# Revit family: Gira_289300
name_source: partatom
category: Electrical Fixtures
revit_build: Autodesk Revit 2017 (Build: 20160225_1515(x64)
units: mm (PartAtom-declared; Revit-internal decimal feet)

## family parameters
Cut with Voids When Loaded = No
Host = Face
Maintain Annotation Orientation = No
Part Type = Normal
Room Calculation Point = No
Round Connector Dimension = Use Diameter
Shared = No

## types (1)
- FM install.box 3-g Gira E22
    Available = No
    BIM (1) = https://media.stage.bim.site
    Category = Spare part for domestic switching devices
    Data sheet (1) = https://katalog.gira.de
    Default Elevation = 1219 mm
    Description = FM inst.box 3g E22,Gira E2, Gira E22 flush-mounted installation box,,3-gang,Features:,- Installation in brickwork by mounting the installation box, e.g. securing it with plaster. Installation of the device box in the flush-mounted installation box like in a common cavity box.
    GTIN = 4010337049807
    HAN = 289300
    HeinzeBIM = https://bimportal.heinze.de
    Manufacturer = Gira
    Manufacturer URL = https://www.gira.de
    Name = FM install.box 3-g Gira E22
    URL = http://katalog.gira.de

## geometry (parser evidence)
native form markers: Blend x2, Sweep x2
no freeform markers — native parametric forms only
